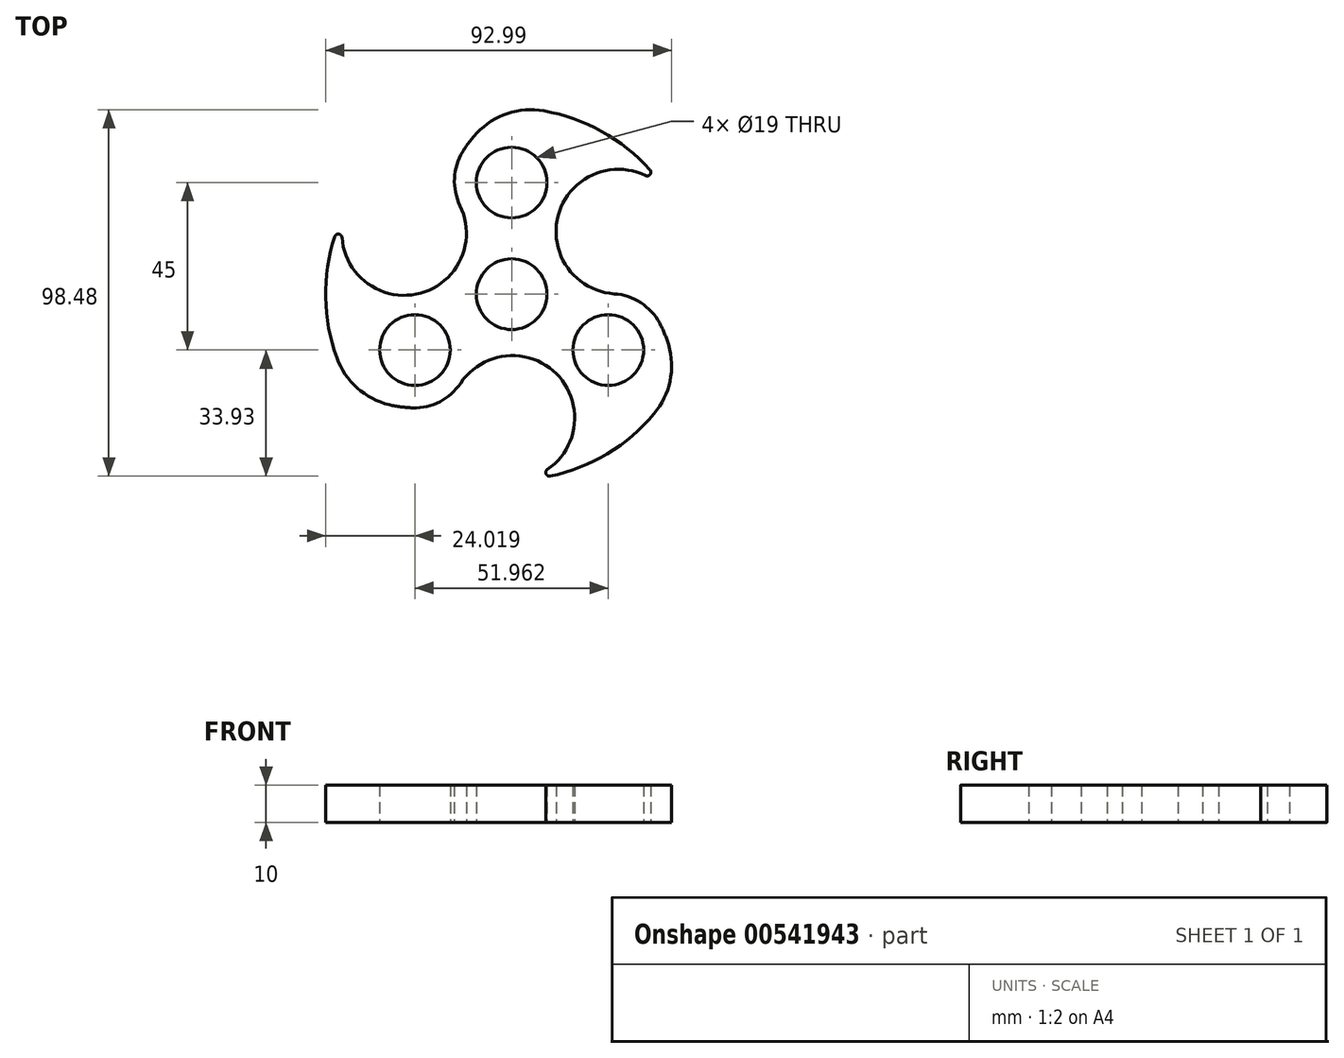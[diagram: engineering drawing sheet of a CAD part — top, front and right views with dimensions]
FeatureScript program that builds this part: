
annotation { "Feature Type Name" : "Feature", "Feature Type Description" : "" }
export const myFeature = defineFeature(function(context is Context, id is Id, definition is map)
    precondition{}
    {
        {
            var Q0;
            Q0=qCreatedBy(makeId("Top.planeOp"),FACE);
            var sketch = newSketch(context, id + "F0", { "sketchPlane" : qUnion([Q0])});
            skArc(sketch, "E0", {"start": v(-47.55, 15.45) * mm, "mid": v(-50, -0.88) * mm, "end": v(-46.98, -17.12) * mm});
            skCircle(sketch, "E1", {"center": v(0, 0) * mm, "radius": 9.5 * mm});
            skPoint(sketch, "E2", {"position": v(0, 16.5) * mm});
            skPoint(sketch, "E3", {"position": v(16.5, 0) * mm});
            skPoint(sketch, "E4", {"position": v(0, -16.5) * mm});
            skPoint(sketch, "E5", {"position": v(-16.5, 0) * mm});
            skCircle(sketch, "E6", {"center": v(0, 30) * mm, "radius": 9.5 * mm});
            skCircle(sketch, "E7.1.0", {"center": v(-25.98, -15) * mm, "radius": 9.5 * mm});
            skCircle(sketch, "E7.2.0", {"center": v(25.98, -15) * mm, "radius": 9.5 * mm});
            skLineSegment(sketch, "E8.2.0", {"start": v(0, -16.5) * mm, "end": v(0, -50) * mm});
            skArc(sketch, "E9", {"start": v(-9.3, 43.31) * mm, "mid": v(-11.37, 40.9) * mm, "end": v(-13.17, 38.3) * mm});
            skPoint(sketch, "E9.first.point", {"position": v(-14.29, 8.25) * mm});
            skPoint(sketch, "E9.third.point", {"position": v(0, 50) * mm});
            skArc(sketch, "E10.1.0", {"start": v(-32.85, -29.72) * mm, "mid": v(-29.74, -30.3) * mm, "end": v(-26.58, -30.55) * mm});
            skArc(sketch, "E10.2.0", {"start": v(42.16, -13.6) * mm, "mid": v(41.1, -10.6) * mm, "end": v(39.75, -7.74) * mm});
            skArc(sketch, "E11.trimOffspring", {"start": v(10.4, -48.9) * mm, "mid": v(25.76, -42.86) * mm, "end": v(38.31, -32.13) * mm});
            skArc(sketch, "E12.trimOffspring", {"start": v(37.16, 33.45) * mm, "mid": v(24.23, 43.73) * mm, "end": v(8.67, 49.24) * mm});
            skArc(sketch, "E13", {"start": v(35.98, 31.89) * mm, "mid": v(12.5, 21.09) * mm, "end": v(27.56, 0.09) * mm});
            skArc(sketch, "E14.1.0", {"start": v(-45.6, 15.22) * mm, "mid": v(-24.51, 0.28) * mm, "end": v(-13.86, 23.83) * mm});
            skArc(sketch, "E14.2.0", {"start": v(9.62, -47.1) * mm, "mid": v(12.01, -21.37) * mm, "end": v(-13.7, -23.91) * mm});
            skPoint(sketch, "E15.visualSharp", {"position": v(43.3, 25) * mm});
            skArc(sketch, "E15.filletArc", {"start": v(35.98, 31.89) * mm, "mid": v(37.22, 32.19) * mm, "end": v(37.16, 33.45) * mm});
            skArc(sketch, "E16.filletArc", {"start": v(0.23, 50) * mm, "mid": v(0, 49.98) * mm, "end": v(-0.2, 49.9) * mm});
            skArc(sketch, "E17.filletArc", {"start": v(0.71, 50) * mm, "mid": v(0, 49.92) * mm, "end": v(-0.66, 49.69) * mm});
            skArc(sketch, "E18.filletArc", {"start": v(8.67, 49.24) * mm, "mid": v(-1.07, 48.54) * mm, "end": v(-9.3, 43.31) * mm});
            skPoint(sketch, "E19.visualSharp", {"position": v(-17.1, 28.33) * mm});
            skArc(sketch, "E19.filletArc", {"start": v(-16.78, 29.72) * mm, "mid": v(-16.79, 28.5) * mm, "end": v(-16.23, 27.4) * mm});
            skArc(sketch, "E20.filletArc", {"start": v(-13.17, 38.3) * mm, "mid": v(-15.37, 31.15) * mm, "end": v(-13.86, 23.83) * mm});
            skPoint(sketch, "E21.visualSharp", {"position": v(-16, -28.97) * mm});
            skArc(sketch, "E21.filletArc", {"start": v(-26.58, -30.55) * mm, "mid": v(-19.29, -28.89) * mm, "end": v(-13.7, -23.91) * mm});
            skPoint(sketch, "E22.visualSharp", {"position": v(33.08, 0.64) * mm});
            skArc(sketch, "E22.filletArc", {"start": v(39.75, -7.74) * mm, "mid": v(34.66, -2.26) * mm, "end": v(27.56, 0.09) * mm});
            skPoint(sketch, "E23.visualSharp", {"position": v(43.3, -25) * mm});
            skArc(sketch, "E23.filletArc", {"start": v(38.31, -32.13) * mm, "mid": v(42.57, -23.34) * mm, "end": v(42.16, -13.6) * mm});
            skPoint(sketch, "E24.visualSharp", {"position": v(-43.3, -25) * mm});
            skArc(sketch, "E24.filletArc", {"start": v(-46.98, -17.12) * mm, "mid": v(-41.5, -25.2) * mm, "end": v(-32.85, -29.72) * mm});
            skPoint(sketch, "E25.visualSharp", {"position": v(-43.3, 25) * mm});
            skArc(sketch, "E25.filletArc", {"start": v(-45.6, 15.22) * mm, "mid": v(-46.48, 16.14) * mm, "end": v(-47.55, 15.45) * mm});
            skPoint(sketch, "E26.visualSharp", {"position": v(0, -50) * mm});
            skArc(sketch, "E26.filletArc", {"start": v(9.62, -47.1) * mm, "mid": v(9.27, -48.32) * mm, "end": v(10.4, -48.9) * mm});
            skSolve(sketch);
        }
        {
            var Q0;
            Q0 = qSketchRegion(id + "F0", true);
            extrude(context, id + "F1", {"entities" : qUnion([Q0]), "depth" : 10 * mm, "offsetDistance" : 25 * mm});
        }
    });
